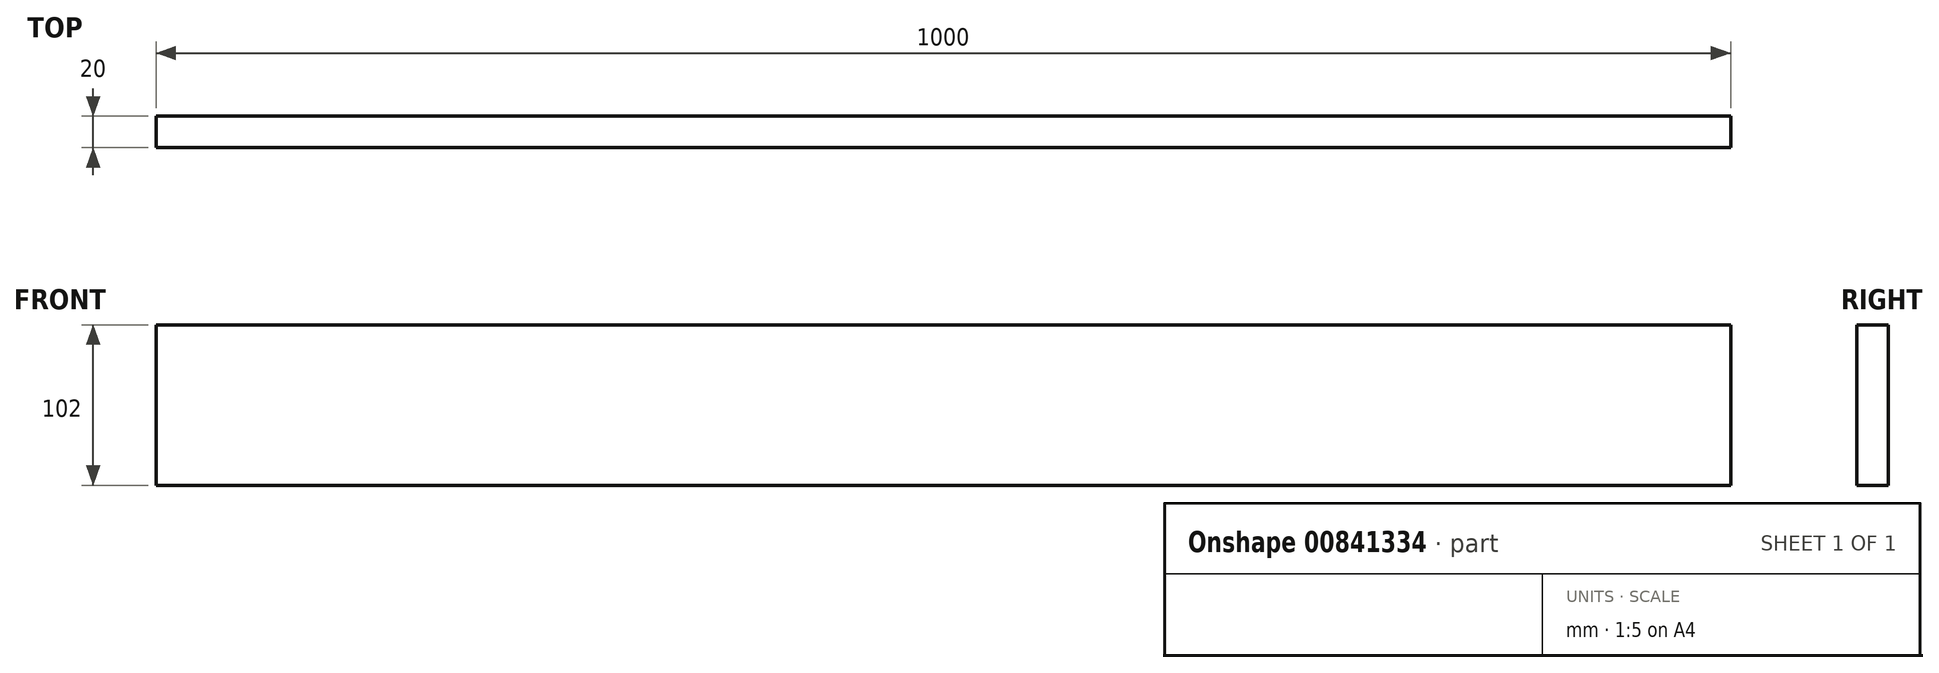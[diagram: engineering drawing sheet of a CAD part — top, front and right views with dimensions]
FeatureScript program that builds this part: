
annotation { "Feature Type Name" : "Feature", "Feature Type Description" : "" }
export const myFeature = defineFeature(function(context is Context, id is Id, definition is map)
    precondition{}
    {
        {
            var Q0;
            Q0=qCreatedBy(makeId("Front.planeOp"),FACE);
            var sketch = newSketch(context, id + "F0", { "sketchPlane" : qUnion([Q0])});
            skLineSegment(sketch, "E0.bottom", {"start": v(-500, -51) * mm, "end": v(500, -51) * mm});
            skLineSegment(sketch, "E0.top", {"start": v(-500, 51) * mm, "end": v(500, 51) * mm});
            skLineSegment(sketch, "E0.left", {"start": v(-500, -51) * mm, "end": v(-500, 51) * mm});
            skLineSegment(sketch, "E0.right", {"start": v(500, -51) * mm, "end": v(500, 51) * mm});
            skLineSegment(sketch, "E1", {"start": v(-500, 0) * mm, "end": v(500, 0) * mm, "construction": true});
            skSolve(sketch);
        }
        {
            var Q0;
            Q0=qSketchRegion(id+"F0",true);
            extrude(context, id + "F1", {"entities" : qUnion([Q0]), "depth" : 20 * mm, "offsetDistance" : 25 * mm});
        }
    });
